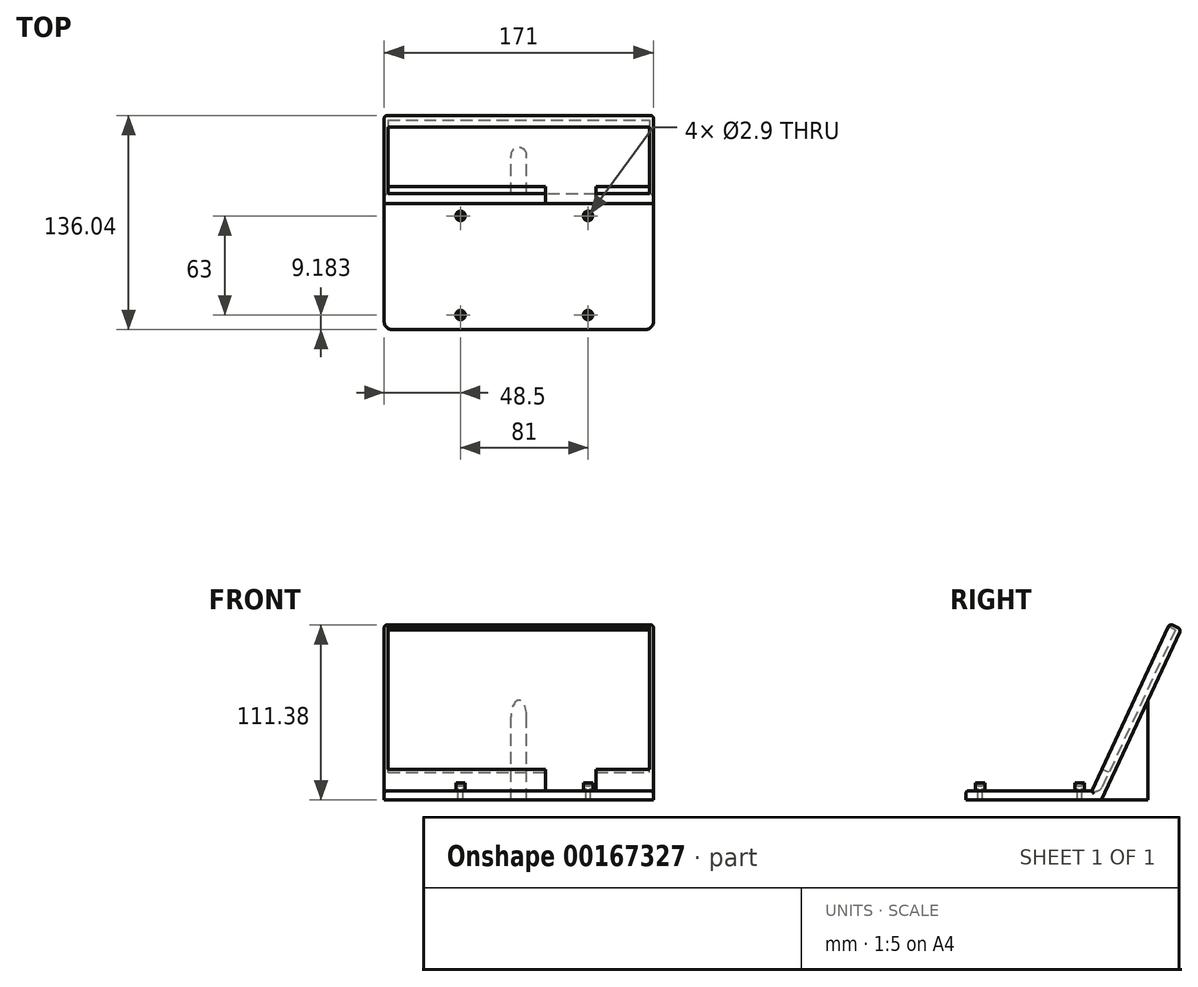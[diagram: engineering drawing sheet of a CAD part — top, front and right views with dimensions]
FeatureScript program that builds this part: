
annotation { "Feature Type Name" : "Feature", "Feature Type Description" : "" }
export const myFeature = defineFeature(function(context is Context, id is Id, definition is map)
    precondition{}
    {
        {
            var Q0;
            Q0=qCreatedBy(makeId("Right.planeOp"),FACE);
            var sketch = newSketch(context, id + "F0", { "sketchPlane" : qUnion([Q0])});
            skLineSegment(sketch, "E0", {"start": v(-47.86, -27.12) * mm, "end": v(38.17, -27.12) * mm});
            skLineSegment(sketch, "E1", {"start": v(38.17, -27.12) * mm, "end": v(88.84, 81.54) * mm});
            skLineSegment(sketch, "E2", {"start": v(88.84, 81.54) * mm, "end": v(81.6, 84.92) * mm});
            skLineSegment(sketch, "E3", {"start": v(81.6, 84.92) * mm, "end": v(32.14, -21.12) * mm});
            skLineSegment(sketch, "E4", {"start": v(32.14, -21.12) * mm, "end": v(-47.86, -21.12) * mm});
            skLineSegment(sketch, "E5", {"start": v(-47.86, -21.12) * mm, "end": v(-47.86, -27.12) * mm});
            skLineSegment(sketch, "E6", {"start": v(38.17, -27.12) * mm, "end": v(67.78, -27.12) * mm});
            skLineSegment(sketch, "E7", {"start": v(67.78, -27.12) * mm, "end": v(67.78, 36.38) * mm});
            skSolve(sketch);
        }
        {
            var Q0;
            Q0=makeQuery(id+"F0.imprint","IMPRINT",FACE,{"disambiguationData":[TD([[makeQuery(id+"F0.imprint","IMPRINT",EDGE,{"derivedFrom":sQuery(id+"F0.wireOp",EDGE,"E0")}),1.0]])]});
            extrude(context, id + "F1", {"entities" : qUnion([Q0]), "depth" : 85.5 * mm, "hasSecondDirection" : true, "secondDirectionOppositeDirection" : true, "secondDirectionDepth" : 85.5 * mm});
        }
        {
            var Q0;
            Q0=makeQuery(id+"F1.opExtrude","SWEPT_FACE",FACE,{"disambiguationData":[OSD([sQuery(id+"F0.wireOp",EDGE,"E3")])]});
            var sketch = newSketch(context, id + "F2", { "sketchPlane" : qUnion([Q0])});
            skLineSegment(sketch, "E8.bottom", {"start": v(-83, 109.44) * mm, "end": v(83, 109.44) * mm});
            skLineSegment(sketch, "E8.top", {"start": v(-83, 9.44) * mm, "end": v(83, 9.44) * mm});
            skLineSegment(sketch, "E8.left", {"start": v(-83, 109.44) * mm, "end": v(-83, 9.44) * mm});
            skLineSegment(sketch, "E8.right", {"start": v(83, 109.44) * mm, "end": v(83, 9.44) * mm});
            skLineSegment(sketch, "E9", {"start": v(49, 9.44) * mm, "end": v(49, -5.56) * mm});
            skLineSegment(sketch, "E10", {"start": v(49, -5.56) * mm, "end": v(17, -5.56) * mm});
            skLineSegment(sketch, "E11", {"start": v(17, -5.56) * mm, "end": v(17, 9.44) * mm});
            skSolve(sketch);
        }
        {
            var Q0;
            Q0=makeQuery(id+"F2.imprint","IMPRINT",FACE,{"disambiguationData":[TD([[makeQuery(id+"F2.imprint","IMPRINT",EDGE,{"derivedFrom":sQuery(id+"F2.wireOp",EDGE,"E8.bottom")}),-1.0]])]});
            var Q1;
            {var subQ0=sQuery(id+"F2.wireOp",EDGE,"E9");Q1=makeQuery(id+"F2.imprint","IMPRINT",FACE,{"disambiguationData":[TD([[makeQuery(id+"F2.imprint","IMPRINT",EDGE,{"derivedFrom":subQ0}),-1.0]])]});}
            extrude(context, id + "F3", {"entities" : qUnion([Q0, Q1]), "operationType" : NewBodyOperationType.REMOVE, "oppositeDirection" : true, "depth" : 5 * mm});
        }
        {
            var Q0;
            Q0=makeQuery(id+"F1.opExtrude","CAP_EDGE",EDGE,{"disambiguationData":[OSD([sQuery(id+"F0.wireOp",EDGE,"E2")])],"isStart":true});
            var Q1;
            Q1=makeQuery(id+"F1.opExtrude","CAP_EDGE",EDGE,{"disambiguationData":[OSD([sQuery(id+"F0.wireOp",EDGE,"E2")])],"isStart":false});
            var Q2;
            Q2=makeQuery(id+"F1.opExtrude","CAP_EDGE",EDGE,{"disambiguationData":[OSD([sQuery(id+"F0.wireOp",EDGE,"E1")])],"isStart":false});
            var Q3;
            Q3=makeQuery(id+"F1.opExtrude","SWEPT_EDGE",EDGE,{"disambiguationData":[OSD([sQuery(id+"F0.wireOp",EDGE,"E1"),sQuery(id+"F0.wireOp",EDGE,"E2")])]});
            var Q4;
            Q4=makeQuery(id+"F1.opExtrude","CAP_EDGE",EDGE,{"disambiguationData":[OSD([sQuery(id+"F0.wireOp",EDGE,"E1")])],"isStart":true});
            var Q5;
            Q5=makeQuery(id+"F1.opExtrude","CAP_EDGE",EDGE,{"disambiguationData":[OSD([sQuery(id+"F0.wireOp",EDGE,"E3")])],"isStart":false});
            var Q6;
            Q6=makeQuery(id+"F1.opExtrude","CAP_EDGE",EDGE,{"disambiguationData":[OSD([sQuery(id+"F0.wireOp",EDGE,"E4")])],"isStart":false});
            var Q7;
            Q7=makeQuery(id+"F1.opExtrude","SWEPT_EDGE",EDGE,{"disambiguationData":[OSD([sQuery(id+"F0.wireOp",EDGE,"E4"),sQuery(id+"F0.wireOp",EDGE,"E5")])]});
            var Q8;
            Q8=makeQuery(id+"F1.opExtrude","CAP_EDGE",EDGE,{"disambiguationData":[OSD([sQuery(id+"F0.wireOp",EDGE,"E4")])],"isStart":true});
            var Q9;
            Q9=makeQuery(id+"F1.opExtrude","SWEPT_EDGE",EDGE,{"disambiguationData":[OSD([sQuery(id+"F0.wireOp",EDGE,"E2"),sQuery(id+"F0.wireOp",EDGE,"E3")])]});
            var Q10;
            Q10=makeQuery(id+"F1.opExtrude","CAP_EDGE",EDGE,{"disambiguationData":[OSD([sQuery(id+"F0.wireOp",EDGE,"E3")])],"isStart":true});
            fillet(context, id + "F4", {"entities" : qUnion([Q0, Q1, Q2, Q3, Q4, Q5, Q6, Q7, Q8, Q9, Q10]), "radius" : 2 * mm, "tangentPropagation" : true, "allowEdgeOverflow" : false});
        }
        {
            var Q0;
            Q0=makeQuery(id+"F1.opExtrude","SWEPT_FACE",FACE,{"disambiguationData":[OSD([sQuery(id+"F0.wireOp",EDGE,"E4")])]});
            var sketch = newSketch(context, id + "F5", { "sketchPlane" : qUnion([Q0])});
            skLineSegment(sketch, "E12.bottom", {"start": v(-40.5, 27.82) * mm, "end": v(47.5, 27.82) * mm});
            skLineSegment(sketch, "E12.top", {"start": v(-40.5, -42.18) * mm, "end": v(47.5, -42.18) * mm});
            skLineSegment(sketch, "E12.left", {"start": v(-40.5, 27.82) * mm, "end": v(-40.5, -42.18) * mm});
            skLineSegment(sketch, "E12.right", {"start": v(47.5, 27.82) * mm, "end": v(47.5, -42.18) * mm});
            skLineSegment(sketch, "E13.bottom", {"start": v(-37, 24.32) * mm, "end": v(44, 24.32) * mm});
            skLineSegment(sketch, "E13.top", {"start": v(-37, -38.68) * mm, "end": v(44, -38.68) * mm});
            skLineSegment(sketch, "E13.left", {"start": v(-37, 24.32) * mm, "end": v(-37, -38.68) * mm});
            skLineSegment(sketch, "E13.right", {"start": v(44, 24.32) * mm, "end": v(44, -38.68) * mm});
            skCircle(sketch, "E14", {"center": v(44, 24.32) * mm, "radius": 3 * mm});
            skCircle(sketch, "E15", {"center": v(44, 24.32) * mm, "radius": 1.45 * mm});
            skCircle(sketch, "E16", {"center": v(44, -38.68) * mm, "radius": 3 * mm});
            skCircle(sketch, "E17", {"center": v(44, -38.68) * mm, "radius": 1.45 * mm});
            skCircle(sketch, "E18", {"center": v(-37, -38.68) * mm, "radius": 3 * mm});
            skCircle(sketch, "E19", {"center": v(-37, -38.68) * mm, "radius": 1.45 * mm});
            skCircle(sketch, "E20", {"center": v(-37, 24.32) * mm, "radius": 3 * mm});
            skCircle(sketch, "E21", {"center": v(-37, 24.32) * mm, "radius": 1.45 * mm});
            skSolve(sketch);
        }
        {
            var Q0;
            {var subQ0=sQuery(id+"F5.wireOp",EDGE,"E13.right");var subQ1=sQuery(id+"F5.wireOp",EDGE,"E13.bottom");var subQ2=makeQuery(id+"F5.imprint","INTERSECT",VERTEX,{"derivedFrom":[subQ1,subQ0]});Q0=makeQuery(id+"F5.imprint","IMPRINT",FACE,{"disambiguationData":[TD([[makeQuery(id+"F5.imprint","IMPRINT",EDGE,{"disambiguationData":[TD([[subQ2,1.0]])],"derivedFrom":subQ1}),1.0]])]});}
            var Q1;
            {var subQ0=sQuery(id+"F5.wireOp",EDGE,"E13.right");var subQ1=sQuery(id+"F5.wireOp",EDGE,"E13.bottom");var subQ2=makeQuery(id+"F5.imprint","INTERSECT",VERTEX,{"derivedFrom":[subQ1,subQ0]});Q1=makeQuery(id+"F5.imprint","IMPRINT",FACE,{"disambiguationData":[TD([[makeQuery(id+"F5.imprint","IMPRINT",EDGE,{"disambiguationData":[TD([[subQ2,1.0]])],"derivedFrom":subQ1}),-1.0]])]});}
            var Q2;
            {var subQ0=sQuery(id+"F5.wireOp",EDGE,"E13.left");var subQ1=sQuery(id+"F5.wireOp",EDGE,"E13.bottom");var subQ2=makeQuery(id+"F5.imprint","INTERSECT",VERTEX,{"derivedFrom":[subQ1,subQ0]});Q2=makeQuery(id+"F5.imprint","IMPRINT",FACE,{"disambiguationData":[TD([[makeQuery(id+"F5.imprint","IMPRINT",EDGE,{"disambiguationData":[TD([[subQ2,-1.0]])],"derivedFrom":subQ1}),1.0]])]});}
            var Q3;
            {var subQ0=sQuery(id+"F5.wireOp",EDGE,"E13.left");var subQ1=sQuery(id+"F5.wireOp",EDGE,"E13.bottom");var subQ2=makeQuery(id+"F5.imprint","INTERSECT",VERTEX,{"derivedFrom":[subQ1,subQ0]});Q3=makeQuery(id+"F5.imprint","IMPRINT",FACE,{"disambiguationData":[TD([[makeQuery(id+"F5.imprint","IMPRINT",EDGE,{"disambiguationData":[TD([[subQ2,-1.0]])],"derivedFrom":subQ1}),-1.0]])]});}
            var Q4;
            {var subQ0=sQuery(id+"F5.wireOp",EDGE,"E13.left");var subQ1=sQuery(id+"F5.wireOp",EDGE,"E13.top");var subQ2=makeQuery(id+"F5.imprint","INTERSECT",VERTEX,{"derivedFrom":[subQ1,subQ0]});Q4=makeQuery(id+"F5.imprint","IMPRINT",FACE,{"disambiguationData":[TD([[makeQuery(id+"F5.imprint","IMPRINT",EDGE,{"disambiguationData":[TD([[subQ2,-1.0]])],"derivedFrom":subQ1}),-1.0]])]});}
            var Q5;
            {var subQ0=sQuery(id+"F5.wireOp",EDGE,"E13.left");var subQ1=sQuery(id+"F5.wireOp",EDGE,"E13.top");var subQ2=makeQuery(id+"F5.imprint","INTERSECT",VERTEX,{"derivedFrom":[subQ1,subQ0]});Q5=makeQuery(id+"F5.imprint","IMPRINT",FACE,{"disambiguationData":[TD([[makeQuery(id+"F5.imprint","IMPRINT",EDGE,{"disambiguationData":[TD([[subQ2,-1.0]])],"derivedFrom":subQ1}),1.0]])]});}
            var Q6;
            {var subQ0=sQuery(id+"F5.wireOp",EDGE,"E13.right");var subQ1=sQuery(id+"F5.wireOp",EDGE,"E13.top");var subQ2=makeQuery(id+"F5.imprint","INTERSECT",VERTEX,{"derivedFrom":[subQ1,subQ0]});Q6=makeQuery(id+"F5.imprint","IMPRINT",FACE,{"disambiguationData":[TD([[makeQuery(id+"F5.imprint","IMPRINT",EDGE,{"disambiguationData":[TD([[subQ2,1.0]])],"derivedFrom":subQ1}),-1.0]])]});}
            var Q7;
            {var subQ0=sQuery(id+"F5.wireOp",EDGE,"E13.right");var subQ1=sQuery(id+"F5.wireOp",EDGE,"E13.top");var subQ2=makeQuery(id+"F5.imprint","INTERSECT",VERTEX,{"derivedFrom":[subQ1,subQ0]});Q7=makeQuery(id+"F5.imprint","IMPRINT",FACE,{"disambiguationData":[TD([[makeQuery(id+"F5.imprint","IMPRINT",EDGE,{"disambiguationData":[TD([[subQ2,1.0]])],"derivedFrom":subQ1}),1.0]])]});}
            extrude(context, id + "F6", {"entities" : qUnion([Q0, Q1, Q2, Q3, Q4, Q5, Q6, Q7]), "operationType" : NewBodyOperationType.REMOVE, "endBound" : BoundingType.THROUGH_ALL, "oppositeDirection" : true, "depth" : 5 * mm});
        }
        {
            var Q0;
            {var subQ0=sQuery(id+"F5.wireOp",EDGE,"E21");var subQ1=sQuery(id+"F5.wireOp",EDGE,"E13.bottom");var subQ2=makeQuery(id+"F5.imprint","INTERSECT",VERTEX,{"derivedFrom":[subQ1,subQ0]});Q0=makeQuery(id+"F5.imprint","IMPRINT",FACE,{"disambiguationData":[TD([[makeQuery(id+"F5.imprint","IMPRINT",EDGE,{"disambiguationData":[TD([[subQ2,-1.0]])],"derivedFrom":subQ1}),1.0]])]});}
            var Q1;
            {var subQ0=sQuery(id+"F5.wireOp",EDGE,"E21");var subQ1=sQuery(id+"F5.wireOp",EDGE,"E13.bottom");var subQ2=makeQuery(id+"F5.imprint","INTERSECT",VERTEX,{"derivedFrom":[subQ1,subQ0]});Q1=makeQuery(id+"F5.imprint","IMPRINT",FACE,{"disambiguationData":[TD([[makeQuery(id+"F5.imprint","IMPRINT",EDGE,{"disambiguationData":[TD([[subQ2,-1.0]])],"derivedFrom":subQ1}),-1.0]])]});}
            var Q2;
            {var subQ0=sQuery(id+"F5.wireOp",EDGE,"E14");var subQ1=sQuery(id+"F5.wireOp",EDGE,"E13.bottom");var subQ2=makeQuery(id+"F5.imprint","INTERSECT",VERTEX,{"derivedFrom":[subQ1,subQ0]});Q2=makeQuery(id+"F5.imprint","IMPRINT",FACE,{"disambiguationData":[TD([[makeQuery(id+"F5.imprint","IMPRINT",EDGE,{"disambiguationData":[TD([[subQ2,-1.0]])],"derivedFrom":subQ1}),1.0]])]});}
            var Q3;
            {var subQ0=sQuery(id+"F5.wireOp",EDGE,"E14");var subQ1=sQuery(id+"F5.wireOp",EDGE,"E13.bottom");var subQ2=makeQuery(id+"F5.imprint","INTERSECT",VERTEX,{"derivedFrom":[subQ1,subQ0]});Q3=makeQuery(id+"F5.imprint","IMPRINT",FACE,{"disambiguationData":[TD([[makeQuery(id+"F5.imprint","IMPRINT",EDGE,{"disambiguationData":[TD([[subQ2,-1.0]])],"derivedFrom":subQ1}),-1.0]])]});}
            var Q4;
            {var subQ0=sQuery(id+"F5.wireOp",EDGE,"E19");var subQ1=sQuery(id+"F5.wireOp",EDGE,"E13.top");var subQ2=makeQuery(id+"F5.imprint","INTERSECT",VERTEX,{"derivedFrom":[subQ1,subQ0]});Q4=makeQuery(id+"F5.imprint","IMPRINT",FACE,{"disambiguationData":[TD([[makeQuery(id+"F5.imprint","IMPRINT",EDGE,{"disambiguationData":[TD([[subQ2,-1.0]])],"derivedFrom":subQ1}),1.0]])]});}
            var Q5;
            {var subQ0=sQuery(id+"F5.wireOp",EDGE,"E19");var subQ1=sQuery(id+"F5.wireOp",EDGE,"E13.top");var subQ2=makeQuery(id+"F5.imprint","INTERSECT",VERTEX,{"derivedFrom":[subQ1,subQ0]});Q5=makeQuery(id+"F5.imprint","IMPRINT",FACE,{"disambiguationData":[TD([[makeQuery(id+"F5.imprint","IMPRINT",EDGE,{"disambiguationData":[TD([[subQ2,-1.0]])],"derivedFrom":subQ1}),-1.0]])]});}
            var Q6;
            {var subQ0=sQuery(id+"F5.wireOp",EDGE,"E16");var subQ1=sQuery(id+"F5.wireOp",EDGE,"E13.top");var subQ2=makeQuery(id+"F5.imprint","INTERSECT",VERTEX,{"derivedFrom":[subQ1,subQ0]});Q6=makeQuery(id+"F5.imprint","IMPRINT",FACE,{"disambiguationData":[TD([[makeQuery(id+"F5.imprint","IMPRINT",EDGE,{"disambiguationData":[TD([[subQ2,-1.0]])],"derivedFrom":subQ1}),1.0]])]});}
            var Q7;
            {var subQ0=sQuery(id+"F5.wireOp",EDGE,"E16");var subQ1=sQuery(id+"F5.wireOp",EDGE,"E13.top");var subQ2=makeQuery(id+"F5.imprint","INTERSECT",VERTEX,{"derivedFrom":[subQ1,subQ0]});Q7=makeQuery(id+"F5.imprint","IMPRINT",FACE,{"disambiguationData":[TD([[makeQuery(id+"F5.imprint","IMPRINT",EDGE,{"disambiguationData":[TD([[subQ2,-1.0]])],"derivedFrom":subQ1}),-1.0]])]});}
            extrude(context, id + "F7", {"entities" : qUnion([Q0, Q1, Q2, Q3, Q4, Q5, Q6, Q7]), "operationType" : NewBodyOperationType.ADD, "depth" : 5 * mm});
        }
        {
            var Q0;
            {var subQ0=sQuery(id+"F0.wireOp",EDGE,"E6");Q0=makeQuery(id+"F0.imprint","IMPRINT",FACE,{"disambiguationData":[TD([[makeQuery(id+"F0.imprint","IMPRINT",EDGE,{"derivedFrom":subQ0}),1.0]])]});}
            extrude(context, id + "F8", {"entities" : qUnion([Q0]), "operationType" : NewBodyOperationType.ADD, "depth" : 5 * mm, "hasSecondDirection" : true, "secondDirectionOppositeDirection" : true, "secondDirectionDepth" : 5 * mm});
        }
        {
            var Q0;
            Q0=makeQuery(id+"F8.opExtrude","CAP_EDGE",EDGE,{"disambiguationData":[OSD([sQuery(id+"F0.wireOp",EDGE,"E7")])],"isStart":false});
            var Q1;
            Q1=makeQuery(id+"F8.opExtrude","CAP_EDGE",EDGE,{"disambiguationData":[OSD([sQuery(id+"F0.wireOp",EDGE,"E7")])],"isStart":true});
            fillet(context, id + "F9", {"entities" : qUnion([Q0, Q1]), "radius" : 5 * mm, "tangentPropagation" : true, "allowEdgeOverflow" : false});
        }
        {
            var Q0;
            Q0=makeQuery(id+"F3.boolean.opBoolean","COPY",EDGE,{"derivedFrom":makeQuery(id+"F3.opExtrude","CAP_EDGE",EDGE,{"disambiguationData":[OSD([sQuery(id+"F2.wireOp",EDGE,"E10")])],"isStart":false})});
            fillet(context, id + "F10", {"entities" : qUnion([Q0]), "radius" : 5 * mm, "tangentPropagation" : true, "allowEdgeOverflow" : false});
        }
        {
            var Q0;
            Q0=makeQuery(id+"F1.opExtrude","CAP_EDGE",EDGE,{"disambiguationData":[OSD([sQuery(id+"F0.wireOp",EDGE,"E5")])],"isStart":false});
            var Q1;
            Q1=makeQuery(id+"F1.opExtrude","CAP_EDGE",EDGE,{"disambiguationData":[OSD([sQuery(id+"F0.wireOp",EDGE,"E5")])],"isStart":true});
            fillet(context, id + "F11", {"entities" : qUnion([Q0, Q1]), "radius" : 5 * mm, "tangentPropagation" : true, "allowEdgeOverflow" : false});
        }
        {
            var Q0;
            Q0=makeQuery(id+"F7.opExtrude","CAP_EDGE",EDGE,{"disambiguationData":[OSD([sQuery(id+"F5.wireOp",EDGE,"E19")])],"isStart":false});
            var Q1;
            Q1=makeQuery(id+"F7.opExtrude","CAP_EDGE",EDGE,{"disambiguationData":[OSD([sQuery(id+"F5.wireOp",EDGE,"E21")])],"isStart":false});
            var Q2;
            Q2=makeQuery(id+"F7.opExtrude","CAP_EDGE",EDGE,{"disambiguationData":[OSD([sQuery(id+"F5.wireOp",EDGE,"E17")])],"isStart":false});
            var Q3;
            Q3=makeQuery(id+"F7.opExtrude","CAP_EDGE",EDGE,{"disambiguationData":[OSD([sQuery(id+"F5.wireOp",EDGE,"E15")])],"isStart":false});
            chamfer(context, id + "F12", {"entities" : qUnion([Q0, Q1, Q2, Q3]), "chamferType" : ChamferType.TWO_OFFSETS, "width1" : 2 * mm, "oppositeDirection" : false, "width2" : .2 * mm, "tangentPropagation" : true});
        }
    });
